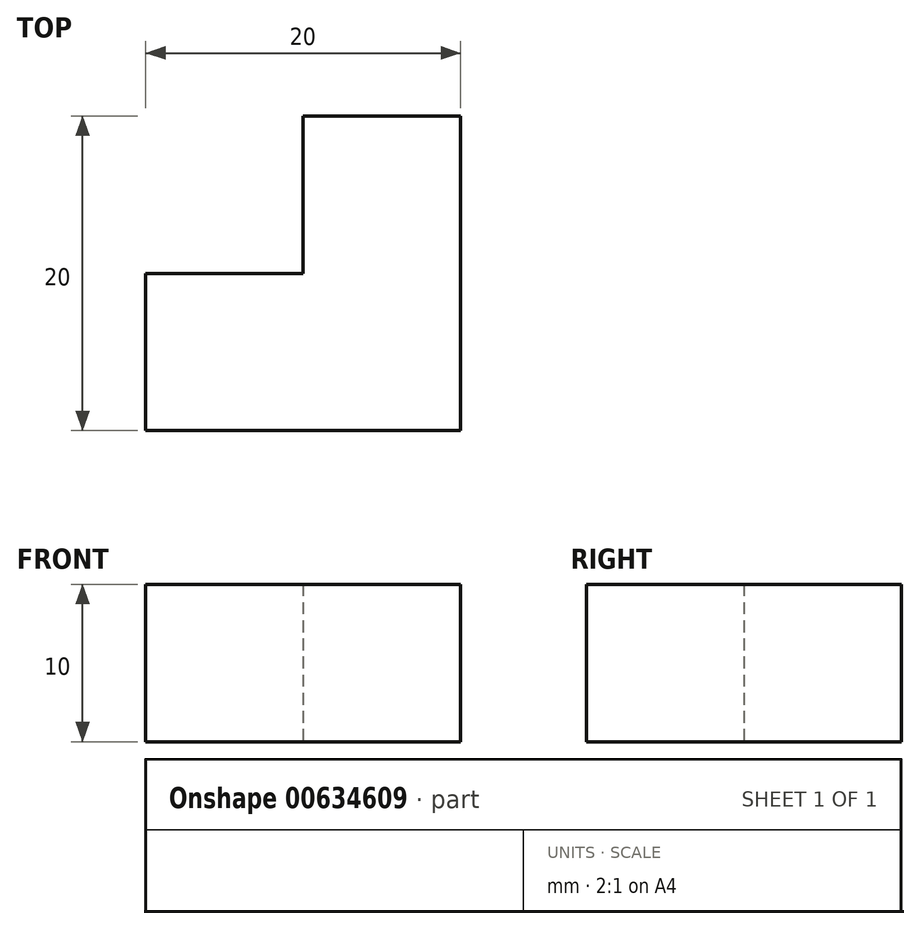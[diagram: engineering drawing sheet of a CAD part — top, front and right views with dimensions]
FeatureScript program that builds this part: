
annotation { "Feature Type Name" : "Feature", "Feature Type Description" : "" }
export const myFeature = defineFeature(function(context is Context, id is Id, definition is map)
    precondition{}
    {
        {
            var Q0;
            Q0=qCreatedBy(makeId("Top.planeOp"),FACE);
            var sketch = newSketch(context, id + "F0", { "sketchPlane" : qUnion([Q0])});
            skLineSegment(sketch, "E0.bottom", {"start": v(0, 0) * mm, "end": v(-20, 0) * mm});
            skLineSegment(sketch, "E0.top", {"start": v(-10, 10) * mm, "end": v(-20, 10) * mm});
            skLineSegment(sketch, "E0.left", {"start": v(0, 0) * mm, "end": v(0, 10) * mm});
            skLineSegment(sketch, "E0.right", {"start": v(-20, 0) * mm, "end": v(-20, 10) * mm});
            skLineSegment(sketch, "E1.top", {"start": v(0, 20) * mm, "end": v(-10, 20) * mm});
            skLineSegment(sketch, "E1.left", {"start": v(0, 10) * mm, "end": v(0, 20) * mm});
            skLineSegment(sketch, "E1.right", {"start": v(-10, 10) * mm, "end": v(-10, 20) * mm});
            skSolve(sketch);
        }
        {
            var Q0;
            Q0 = qSketchRegion(id + "F0", true);
            extrude(context, id + "F1", {"entities" : qUnion([Q0]), "depth" : 10 * mm, "offsetDistance" : 25 * mm});
        }
    });
